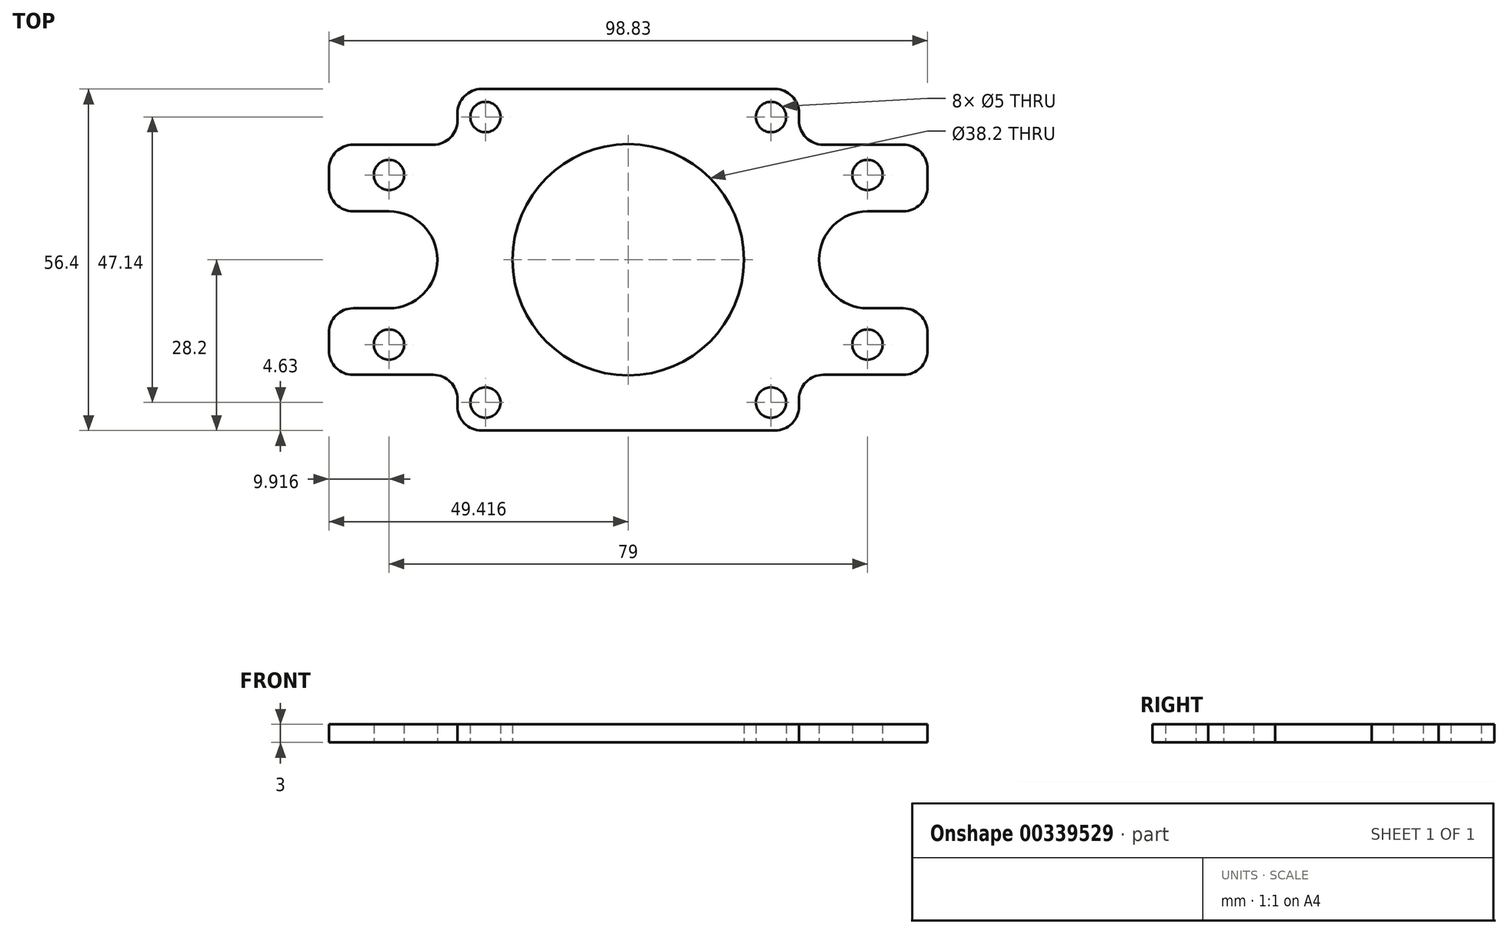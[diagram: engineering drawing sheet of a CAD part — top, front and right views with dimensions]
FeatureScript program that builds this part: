
annotation { "Feature Type Name" : "Feature", "Feature Type Description" : "" }
export const myFeature = defineFeature(function(context is Context, id is Id, definition is map)
    precondition{}
    {
        {
            var Q0;
            Q0=qCreatedBy(makeId("Top.planeOp"),FACE);
            var sketch = newSketch(context, id + "F0", { "sketchPlane" : qUnion([Q0])});
            skCircle(sketch, "E0", {"center": v(-74.55, 24.37) * mm, "radius": 8 * mm});
            skCircle(sketch, "E1", {"center": v(4.45, 24.37) * mm, "radius": 8 * mm});
            skCircle(sketch, "E2", {"center": v(-35.05, 24.37) * mm, "radius": 19.1 * mm});
            skPoint(sketch, "E2.centerSnap0", {"position": v(-35.05, 2.37) * mm});
            skLineSegment(sketch, "E3", {"start": v(-36.73, 43.4) * mm, "end": v(-33.38, 43.4) * mm});
            skLineSegment(sketch, "E4.bottom", {"start": v(-58.62, 0.8) * mm, "end": v(-11.48, 0.8) * mm, "construction": true});
            skLineSegment(sketch, "E4.top", {"start": v(-58.62, 47.94) * mm, "end": v(-11.48, 47.94) * mm, "construction": true});
            skLineSegment(sketch, "E4.left", {"start": v(-58.62, 0.8) * mm, "end": v(-58.62, 47.94) * mm, "construction": true});
            skLineSegment(sketch, "E4.right", {"start": v(-11.48, 0.8) * mm, "end": v(-11.48, 47.94) * mm, "construction": true});
            skLineSegment(sketch, "E5.bottom", {"start": v(-63.25, -3.83) * mm, "end": v(-6.85, -3.83) * mm});
            skLineSegment(sketch, "E5.top", {"start": v(-63.25, 52.57) * mm, "end": v(-6.85, 52.57) * mm});
            skLineSegment(sketch, "E5.left", {"start": v(-63.25, -3.83) * mm, "end": v(-63.25, 52.57) * mm});
            skLineSegment(sketch, "E5.right", {"start": v(-6.85, -3.83) * mm, "end": v(-6.85, 52.57) * mm});
            skCircle(sketch, "E6", {"center": v(-58.62, 47.94) * mm, "radius": 2.5 * mm});
            skCircle(sketch, "E7", {"center": v(-11.48, 47.94) * mm, "radius": 2.5 * mm});
            skCircle(sketch, "E8", {"center": v(-11.48, 0.8) * mm, "radius": 2.5 * mm});
            skCircle(sketch, "E9", {"center": v(-58.62, 0.8) * mm, "radius": 2.5 * mm});
            skLineSegment(sketch, "E10.bottom", {"start": v(-84.47, 43.37) * mm, "end": v(14.36, 43.37) * mm});
            skLineSegment(sketch, "E10.top", {"start": v(-84.47, 5.37) * mm, "end": v(14.36, 5.37) * mm});
            skLineSegment(sketch, "E10.left", {"start": v(-84.47, 43.37) * mm, "end": v(-84.47, 5.37) * mm});
            skLineSegment(sketch, "E10.right", {"start": v(14.36, 43.37) * mm, "end": v(14.36, 5.37) * mm});
            skLineSegment(sketch, "E11", {"start": v(-74.55, 5.37) * mm, "end": v(-74.55, 43.37) * mm, "construction": true});
            skLineSegment(sketch, "E12", {"start": v(4.45, 5.37) * mm, "end": v(4.45, 43.37) * mm, "construction": true});
            skCircle(sketch, "E13", {"center": v(-74.55, 38.37) * mm, "radius": 2.5 * mm});
            skCircle(sketch, "E14", {"center": v(-74.55, 10.37) * mm, "radius": 2.5 * mm});
            skCircle(sketch, "E15", {"center": v(4.45, 10.37) * mm, "radius": 2.5 * mm});
            skCircle(sketch, "E16", {"center": v(4.45, 38.37) * mm, "radius": 2.5 * mm});
            skLineSegment(sketch, "E17", {"start": v(4.45, 16.37) * mm, "end": v(14.36, 16.37) * mm});
            skLineSegment(sketch, "E18", {"start": v(4.45, 32.37) * mm, "end": v(14.36, 32.37) * mm});
            skLineSegment(sketch, "E19", {"start": v(-74.55, 32.37) * mm, "end": v(-84.47, 32.37) * mm});
            skLineSegment(sketch, "E20", {"start": v(-74.55, 16.37) * mm, "end": v(-84.47, 16.37) * mm});
            skLineSegment(sketch, "E21", {"start": v(-74.55, 24.37) * mm, "end": v(4.45, 24.37) * mm, "construction": true});
            skSolve(sketch);
        }
        {
            var Q0;
            {var subQ0=sQuery(id+"F0.wireOp",EDGE,"E10.bottom");var subQ1=sQuery(id+"F0.wireOp",EDGE,"E2");var subQ2=makeQuery(id+"F0.imprint","INTERSECT",VERTEX,{"disambiguationData":[OD(1.0)],"derivedFrom":[subQ1,subQ0]});Q0=makeQuery(id+"F0.imprint","IMPRINT",FACE,{"disambiguationData":[TD([[makeQuery(id+"F0.imprint","IMPRINT",EDGE,{"disambiguationData":[TD([[subQ2,-1.0]])],"derivedFrom":subQ1}),-1.0]])]});}
            var Q1;
            {var subQ0=sQuery(id+"F0.wireOp",EDGE,"E10.bottom");var subQ1=sQuery(id+"F0.wireOp",EDGE,"E2");var subQ2=makeQuery(id+"F0.imprint","INTERSECT",VERTEX,{"disambiguationData":[OD(0.0)],"derivedFrom":[subQ1,subQ0]});Q1=makeQuery(id+"F0.imprint","IMPRINT",FACE,{"disambiguationData":[TD([[makeQuery(id+"F0.imprint","IMPRINT",EDGE,{"disambiguationData":[TD([[subQ2,1.0]])],"derivedFrom":subQ1}),-1.0]])]});}
            var Q2;
            Q2=makeQuery(id+"F0.imprint","IMPRINT",FACE,{"disambiguationData":[TD([[makeQuery(id+"F0.imprint","IMPRINT",EDGE,{"derivedFrom":sQuery(id+"F0.wireOp",EDGE,"E13")}),-1.0]])]});
            var Q3;
            Q3=makeQuery(id+"F0.imprint","IMPRINT",FACE,{"disambiguationData":[TD([[makeQuery(id+"F0.imprint","IMPRINT",EDGE,{"derivedFrom":sQuery(id+"F0.wireOp",EDGE,"E15")}),-1.0]])]});
            var Q4;
            {var subQ1=sQuery(id+"F0.wireOp",EDGE,"E5.bottom");Q4=makeQuery(id+"F0.imprint","IMPRINT",FACE,{"disambiguationData":[TD([[makeQuery(id+"F0.imprint","IMPRINT",EDGE,{"derivedFrom":subQ1}),1.0]])]});}
            var Q5;
            {var subQ0=sQuery(id+"F0.wireOp",EDGE,"E5.top");Q5=makeQuery(id+"F0.imprint","IMPRINT",FACE,{"disambiguationData":[TD([[makeQuery(id+"F0.imprint","IMPRINT",EDGE,{"derivedFrom":subQ0}),-1.0]])]});}
            extrude(context, id + "F1", {"entities" : qUnion([Q0, Q1, Q2, Q3, Q4, Q5]), "depth" : 3 * mm, "offsetDistance" : 25 * mm});
        }
        {
            var Q0;
            Q0=makeQuery(id+"F1.opExtrude","SWEPT_EDGE",EDGE,{"disambiguationData":[OSD([sQuery(id+"F0.wireOp",EDGE,"E5.top"),sQuery(id+"F0.wireOp",EDGE,"E5.right")])]});
            var Q1;
            Q1=makeQuery(id+"F1.opExtrude","SWEPT_EDGE",EDGE,{"disambiguationData":[OSD([sQuery(id+"F0.wireOp",EDGE,"E10.bottom"),sQuery(id+"F0.wireOp",EDGE,"E10.right")])]});
            var Q2;
            Q2=makeQuery(id+"F1.opExtrude","SWEPT_EDGE",EDGE,{"disambiguationData":[OSD([sQuery(id+"F0.wireOp",EDGE,"E10.top"),sQuery(id+"F0.wireOp",EDGE,"E10.right")])]});
            var Q3;
            Q3=makeQuery(id+"F1.opExtrude","SWEPT_EDGE",EDGE,{"disambiguationData":[OSD([sQuery(id+"F0.wireOp",EDGE,"E5.bottom"),sQuery(id+"F0.wireOp",EDGE,"E5.right")])]});
            var Q4;
            Q4=makeQuery(id+"F1.opExtrude","SWEPT_EDGE",EDGE,{"disambiguationData":[OSD([sQuery(id+"F0.wireOp",EDGE,"E5.top"),sQuery(id+"F0.wireOp",EDGE,"E5.left")])]});
            var Q5;
            Q5=makeQuery(id+"F1.opExtrude","SWEPT_EDGE",EDGE,{"disambiguationData":[OSD([sQuery(id+"F0.wireOp",EDGE,"E10.bottom"),sQuery(id+"F0.wireOp",EDGE,"E10.left")])]});
            var Q6;
            Q6=makeQuery(id+"F1.opExtrude","SWEPT_EDGE",EDGE,{"disambiguationData":[OSD([sQuery(id+"F0.wireOp",EDGE,"E10.left"),sQuery(id+"F0.wireOp",EDGE,"E20")])]});
            var Q7;
            Q7=makeQuery(id+"F1.opExtrude","SWEPT_EDGE",EDGE,{"disambiguationData":[OSD([sQuery(id+"F0.wireOp",EDGE,"E10.left"),sQuery(id+"F0.wireOp",EDGE,"E19")])]});
            var Q8;
            Q8=makeQuery(id+"F1.opExtrude","SWEPT_EDGE",EDGE,{"disambiguationData":[OSD([sQuery(id+"F0.wireOp",EDGE,"E10.top"),sQuery(id+"F0.wireOp",EDGE,"E10.left")])]});
            var Q9;
            Q9=makeQuery(id+"F1.opExtrude","SWEPT_EDGE",EDGE,{"disambiguationData":[OSD([sQuery(id+"F0.wireOp",EDGE,"E5.bottom"),sQuery(id+"F0.wireOp",EDGE,"E5.left")])]});
            var Q10;
            Q10=makeQuery(id+"F1.opExtrude","SWEPT_EDGE",EDGE,{"disambiguationData":[OSD([sQuery(id+"F0.wireOp",EDGE,"E10.right"),sQuery(id+"F0.wireOp",EDGE,"E18")])]});
            var Q11;
            Q11=makeQuery(id+"F1.opExtrude","SWEPT_EDGE",EDGE,{"disambiguationData":[OSD([sQuery(id+"F0.wireOp",EDGE,"E10.right"),sQuery(id+"F0.wireOp",EDGE,"E17")])]});
            var Q12;
            Q12=makeQuery(id+"F1.opExtrude","SWEPT_EDGE",EDGE,{"disambiguationData":[OSD([sQuery(id+"F0.wireOp",EDGE,"E5.right"),sQuery(id+"F0.wireOp",EDGE,"E10.bottom")])]});
            var Q13;
            Q13=makeQuery(id+"F1.opExtrude","SWEPT_EDGE",EDGE,{"disambiguationData":[OSD([sQuery(id+"F0.wireOp",EDGE,"E5.right"),sQuery(id+"F0.wireOp",EDGE,"E10.top")])]});
            var Q14;
            Q14=makeQuery(id+"F1.opExtrude","SWEPT_EDGE",EDGE,{"disambiguationData":[OSD([sQuery(id+"F0.wireOp",EDGE,"E5.left"),sQuery(id+"F0.wireOp",EDGE,"E10.top")])]});
            var Q15;
            Q15=makeQuery(id+"F1.opExtrude","SWEPT_EDGE",EDGE,{"disambiguationData":[OSD([sQuery(id+"F0.wireOp",EDGE,"E5.left"),sQuery(id+"F0.wireOp",EDGE,"E10.bottom")])]});
            fillet(context, id + "F2", {"entities" : qUnion([Q0, Q1, Q2, Q3, Q4, Q5, Q6, Q7, Q8, Q9, Q10, Q11, Q12, Q13, Q14, Q15]), "radius" : 4 * mm, "tangentPropagation" : true, "allowEdgeOverflow" : false});
        }
    });
